# Revit family: AFX-Irvine-Pendant
name_source: partatom
category: Lighting Fixtures
units: mm (PartAtom-declared; Revit-internal decimal feet)

## family parameters
Cut with Voids When Loaded = No
Host = Face
Light Source = Yes
Part Type = Normal
Room Calculation Point = No
Round Connector Dimension = Use Diameter
Shared = No

## types (1)
- IRVP05LAJUDBK
    Apparent Load = 0 VA
    Assembly Code = D5020200
    Color Filter = 16777215
    Colour Rendering Index = 80
    Cord Finish = AFX - Black Steel
    Default Elevation = 48"
    Description = Pendant - 12 1/4"Dia x 3 3/4"H
    Diameter = 4 3/4"
    Diffuser Finish = AFX - White Acrylic
    Dimming Lamp Color Temperature Shift = <None>
    Emit Shape Visible in Rendering = No
    Emit from Circle Diameter = 4 3/4"
    Height = 11 1/2"
    Housing Finish = AFX - Black Steel
    Keynote = 12500
    Manufacturer = AFX Inc
    Model = IRVP05LAJUDBK
    Photometric Web File = IRVP05LAJUDBK(3000K).IES
    Power Factor = 1
    Product Documentation Link = https://www.afxinc.com
    Revit File Built By = https://servex-us.com
    Screen Finish = AFX - Black Steel
    Support Finish = AFX - Black Steel
    Sustainability = https://lamprecycle.org
    Tilt Angle = 90.00°
    Type Comments = Irvine
    URL = https://www.afxinc.com
    Voltage = 120 V
    Wattage Comments = 15

## geometry (parser evidence)
native form markers: Sweep x2
no freeform markers — native parametric forms only
